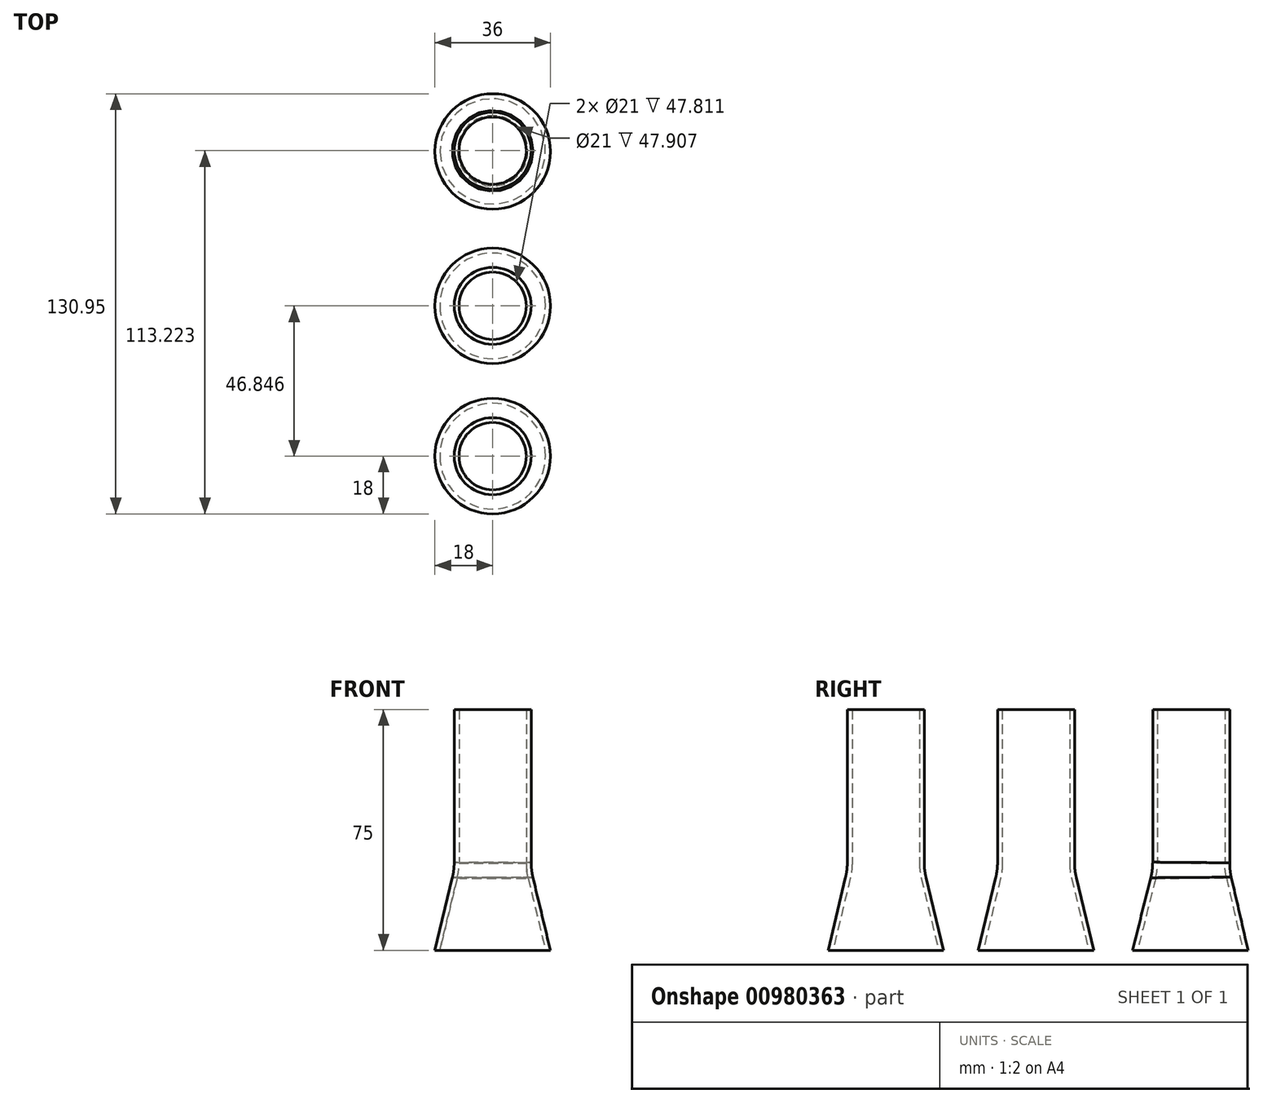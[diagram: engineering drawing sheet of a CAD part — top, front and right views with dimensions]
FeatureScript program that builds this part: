
annotation { "Feature Type Name" : "Feature", "Feature Type Description" : "" }
export const myFeature = defineFeature(function(context is Context, id is Id, definition is map)
    precondition{}
    {
        {
            var Q0;
            Q0=qCreatedBy(makeId("Top.planeOp"),FACE);
            var sketch = newSketch(context, id + "F0", { "sketchPlane" : qUnion([Q0])});
            skCircle(sketch, "E0", {"center": v(0, 0) * mm, "radius": 18 * mm});
            skSolve(sketch);
        }
        {
            var Q0;
            Q0=qCreatedBy(makeId("Top.planeOp"),FACE);
            cPlane(context, id + "F1", {"entities" : qUnion([Q0]), "cplaneType" : CPlaneType.OFFSET, "offset" : 25 * mm, "width" : 150 * mm, "height" : 150 * mm});
        }
        {
            var Q0;
            Q0=qCreatedBy(id+"F1.planeOp",FACE);
            var sketch = newSketch(context, id + "F2", { "sketchPlane" : qUnion([Q0])});
            skCircle(sketch, "E1", {"center": v(0, 0) * mm, "radius": 12 * mm});
            skSolve(sketch);
        }
        {
            var Q0;
            Q0=qCreatedBy(id+"F1.planeOp",FACE);
            cPlane(context, id + "F3", {"entities" : qUnion([Q0]), "cplaneType" : CPlaneType.OFFSET, "offset" : 50 * mm, "width" : 150 * mm, "height" : 150 * mm});
        }
        {
            var Q0;
            Q0 = qSketchRegion(id + "F0", true);
            var Q1;
            Q1 = qSketchRegion(id + "F2", true);
            loft(context, id + "F4", {"sheetProfilesArray" : [{ "sheetProfileEntities" : qUnion([Q0]) }, { "sheetProfileEntities" : qUnion([Q1]) }]});
        }
        {
            var Q0;
            Q0 = qSketchRegion(id + "F2", true);
            var Q1;
            Q1=qCreatedBy(id+"F3.planeOp",FACE);
            extrude(context, id + "F5", {"entities" : qUnion([Q0]), "operationType" : NewBodyOperationType.ADD, "endBound" : BoundingType.UP_TO_SURFACE, "depth" : 25 * mm, "endBoundEntityFace" : qUnion([Q1]), "offsetDistance" : 25 * mm});
        }
        {
            var Q0;
            Q0=makeQuery(id+"F5.opExtrude","CAP_FACE",FACE,{"disambiguationData":[OSD([sQuery(id+"F2.wireOp",EDGE,"E1")])],"isStart":false});
            var Q1;
            Q1=makeQuery(id+"F4.opLoft","CAP_FACE",FACE,{"disambiguationData":[OSD([makeQuery(id+"F0.imprint","IMPRINT",FACE,{"disambiguationData":[TD([[makeQuery(id+"F0.imprint","IMPRINT",EDGE,{"derivedFrom":sQuery(id+"F0.wireOp",EDGE,"E0")}),1.0]])]})])],"isStart":true});
            shell(context, id + "F6", {"entities" : qUnion([Q0, Q1]), "thickness" : 1.5 * mm});
        }
        {
            var Q0;
            Q0=qCreatedBy(makeId("Top.planeOp"),FACE);
            var sketch = newSketch(context, id + "F7", { "sketchPlane" : qUnion([Q0])});
            skCircle(sketch, "E2", {"center": v(0, 46.85) * mm, "radius": 18 * mm});
            skSolve(sketch);
        }
        {
            var Q0;
            Q0=qCreatedBy(id+"F1.planeOp",FACE);
            var sketch = newSketch(context, id + "F8", { "sketchPlane" : qUnion([Q0])});
            skCircle(sketch, "E3", {"center": v(0, 46.85) * mm, "radius": 12 * mm});
            skSolve(sketch);
        }
        {
            var Q0;
            Q0 = qSketchRegion(id + "F7", true);
            var Q1;
            Q1 = qSketchRegion(id + "F8", true);
            loft(context, id + "F9", {"sheetProfilesArray" : [{ "sheetProfileEntities" : qUnion([Q0]) }, { "sheetProfileEntities" : qUnion([Q1]) }]});
        }
        {
            var Q0;
            Q0=makeQuery(id+"F9.opLoft","CAP_FACE",FACE,{"disambiguationData":[OSD([makeQuery(id+"F8.imprint","IMPRINT",FACE,{"disambiguationData":[TD([[makeQuery(id+"F8.imprint","IMPRINT",EDGE,{"derivedFrom":sQuery(id+"F8.wireOp",EDGE,"E3")}),1.0]])]})])],"isStart":true});
            var Q1;
            Q1=qCreatedBy(id+"F3.planeOp",FACE);
            extrude(context, id + "F10", {"entities" : qUnion([Q0]), "operationType" : NewBodyOperationType.ADD, "endBound" : BoundingType.UP_TO_SURFACE, "depth" : 25 * mm, "endBoundEntityFace" : qUnion([Q1]), "offsetDistance" : 25 * mm});
        }
        {
            var Q0;
            Q0=makeQuery(id+"F10.opExtrude","CAP_FACE",FACE,{"disambiguationData":[OSD([makeQuery(id+"F8.imprint","IMPRINT",FACE,{"disambiguationData":[TD([[makeQuery(id+"F8.imprint","IMPRINT",EDGE,{"derivedFrom":sQuery(id+"F8.wireOp",EDGE,"E3")}),1.0]])]})])],"isStart":false});
            var Q1;
            Q1=makeQuery(id+"F9.opLoft","CAP_FACE",FACE,{"disambiguationData":[OSD([makeQuery(id+"F7.imprint","IMPRINT",FACE,{"disambiguationData":[TD([[makeQuery(id+"F7.imprint","IMPRINT",EDGE,{"derivedFrom":sQuery(id+"F7.wireOp",EDGE,"E2")}),1.0]])]})])],"isStart":true});
            shell(context, id + "F11", {"entities" : qUnion([Q0, Q1]), "thickness" : 1.5 * mm});
        }
        {
            var Q0;
            Q0=qCreatedBy(makeId("Top.planeOp"),FACE);
            var sketch = newSketch(context, id + "F12", { "sketchPlane" : qUnion([Q0])});
            skCircle(sketch, "E4", {"center": v(0, 94.95) * mm, "radius": 18 * mm});
            skSolve(sketch);
        }
        {
            var Q0;
            Q0=qCreatedBy(id+"F1.planeOp",FACE);
            var sketch = newSketch(context, id + "F13", { "sketchPlane" : qUnion([Q0])});
            skCircle(sketch, "E5", {"center": v(0, 95.22) * mm, "radius": 12 * mm});
            skSolve(sketch);
        }
        {
            var Q0;
            Q0 = qSketchRegion(id + "F12", true);
            var Q1;
            Q1 = qSketchRegion(id + "F13", true);
            loft(context, id + "F14", {"sheetProfilesArray" : [{ "sheetProfileEntities" : qUnion([Q0]) }, { "sheetProfileEntities" : qUnion([Q1]) }]});
        }
        {
            var Q0;
            Q0 = qSketchRegion(id + "F13", true);
            var Q1;
            Q1=qCreatedBy(id+"F3.planeOp",FACE);
            extrude(context, id + "F15", {"entities" : qUnion([Q0]), "operationType" : NewBodyOperationType.ADD, "endBound" : BoundingType.UP_TO_SURFACE, "depth" : 25 * mm, "endBoundEntityFace" : qUnion([Q1]), "offsetDistance" : 25 * mm});
        }
        {
            var Q0;
            Q0=makeQuery(id+"F14.opLoft","CAP_FACE",FACE,{"disambiguationData":[OSD([makeQuery(id+"F12.imprint","IMPRINT",FACE,{"disambiguationData":[TD([[makeQuery(id+"F12.imprint","IMPRINT",EDGE,{"derivedFrom":sQuery(id+"F12.wireOp",EDGE,"E4")}),1.0]])]})])],"isStart":true});
            var Q1;
            Q1=makeQuery(id+"F15.opExtrude","CAP_FACE",FACE,{"disambiguationData":[OSD([sQuery(id+"F13.wireOp",EDGE,"E5")])],"isStart":false});
            shell(context, id + "F16", {"entities" : qUnion([Q0, Q1]), "thickness" : 1.5 * mm});
        }
        {
            var Q0;
            {var subQ0=sQuery(id+"F2.wireOp",EDGE,"E1");Q0=makeQuery(id+"F5.boolean.opBoolean","MERGE",EDGE,{"derivedFrom":[makeQuery(id+"F4.opLoft","MID_CAP_EDGE",EDGE,{"disambiguationData":[OSD([subQ0])],"capPos":1.0}),makeQuery(id+"F5.opExtrude","CAP_EDGE",EDGE,{"disambiguationData":[OSD([subQ0])],"isStart":true})]});}
            var Q1;
            {var subQ0=sQuery(id+"F2.wireOp",EDGE,"E1");Q1=makeQuery(id+"F6.opShell","OFFSET_EDGE",EDGE,{"disambiguationData":[OSD([subQ0]),TDD([makeQuery(id+"F5.boolean.opBoolean","MERGE",EDGE,{"derivedFrom":[makeQuery(id+"F4.opLoft","MID_CAP_EDGE",EDGE,{"disambiguationData":[OSD([subQ0])],"capPos":1.0}),makeQuery(id+"F5.opExtrude","CAP_EDGE",EDGE,{"disambiguationData":[OSD([subQ0])],"isStart":true})]})])]});}
            var Q2;
            {var subQ0=sQuery(id+"F13.wireOp",EDGE,"E5");Q2=makeQuery(id+"F15.boolean.opBoolean","MERGE",EDGE,{"derivedFrom":[makeQuery(id+"F14.opLoft","MID_CAP_EDGE",EDGE,{"disambiguationData":[OSD([subQ0])],"capPos":1.0}),makeQuery(id+"F15.opExtrude","CAP_EDGE",EDGE,{"disambiguationData":[OSD([subQ0])],"isStart":true})]});}
            var Q3;
            {var subQ0=sQuery(id+"F8.wireOp",EDGE,"E3");Q3=makeQuery(id+"F10.boolean.opBoolean","MERGE",EDGE,{"derivedFrom":[makeQuery(id+"F9.opLoft","MID_CAP_EDGE",EDGE,{"disambiguationData":[OSD([subQ0])],"capPos":1.0}),makeQuery(id+"F10.opExtrude","CAP_EDGE",EDGE,{"disambiguationData":[OSD([subQ0])],"isStart":true})]});}
            var Q4;
            {var subQ0=sQuery(id+"F13.wireOp",EDGE,"E5");Q4=makeQuery(id+"F16.opShell","OFFSET_EDGE",EDGE,{"disambiguationData":[OSD([subQ0]),TDD([makeQuery(id+"F15.boolean.opBoolean","MERGE",EDGE,{"derivedFrom":[makeQuery(id+"F14.opLoft","MID_CAP_EDGE",EDGE,{"disambiguationData":[OSD([subQ0])],"capPos":1.0}),makeQuery(id+"F15.opExtrude","CAP_EDGE",EDGE,{"disambiguationData":[OSD([subQ0])],"isStart":true})]})])]});}
            var Q5;
            {var subQ0=sQuery(id+"F8.wireOp",EDGE,"E3");Q5=makeQuery(id+"F11.opShell","OFFSET_EDGE",EDGE,{"disambiguationData":[OSD([subQ0]),TDD([makeQuery(id+"F10.boolean.opBoolean","MERGE",EDGE,{"derivedFrom":[makeQuery(id+"F9.opLoft","MID_CAP_EDGE",EDGE,{"disambiguationData":[OSD([subQ0])],"capPos":1.0}),makeQuery(id+"F10.opExtrude","CAP_EDGE",EDGE,{"disambiguationData":[OSD([subQ0])],"isStart":true})]})])]});}
            fillet(context, id + "F17", {"entities" : qUnion([Q0, Q1, Q2, Q3, Q4, Q5]), "radius" : 20 * mm, "tangentPropagation" : true, "allowEdgeOverflow" : false});
        }
        {
            var Q0;
            Q0=qCreatedBy(makeId("Top.planeOp"),FACE);
            var sketch = newSketch(context, id + "F18", { "sketchPlane" : qUnion([Q0])});
            skLineSegment(sketch, "E6.bottom", {"start": v(19.85, 118.64) * mm, "end": v(-19.85, 118.64) * mm});
            skLineSegment(sketch, "E6.top", {"start": v(19.85, -24.56) * mm, "end": v(-19.85, -24.56) * mm});
            skLineSegment(sketch, "E6.left", {"start": v(19.85, 118.64) * mm, "end": v(19.85, -24.56) * mm});
            skLineSegment(sketch, "E6.right", {"start": v(-19.85, 118.64) * mm, "end": v(-19.85, -24.56) * mm});
            skPoint(sketch, "E6.middle", {"position": v(0, 47.04) * mm});
            skSolve(sketch);
        }
        {
            var Q0;
            Q0 = qSketchRegion(id + "F18", true);
            extrude(context, id + "F19", {"entities" : qUnion([Q0]), "depth" : 2 * mm, "offsetDistance" : 25 * mm});
        }
        {
            var Q0;
            Q0=makeQuery(id+"F4.opLoft","SWEPT_BODY",BODY,{"disambiguationData":[OSD([makeQuery(id+"F0.imprint","IMPRINT",FACE,{"disambiguationData":[TD([[makeQuery(id+"F0.imprint","IMPRINT",EDGE,{"derivedFrom":sQuery(id+"F0.wireOp",EDGE,"E0")}),1.0]])]}),makeQuery(id+"F2.imprint","IMPRINT",FACE,{"disambiguationData":[TD([[makeQuery(id+"F2.imprint","IMPRINT",EDGE,{"derivedFrom":sQuery(id+"F2.wireOp",EDGE,"E1")}),1.0]])]})])]});
            var Q1;
            Q1=makeQuery(id+"F9.opLoft","SWEPT_BODY",BODY,{"disambiguationData":[OSD([makeQuery(id+"F7.imprint","IMPRINT",FACE,{"disambiguationData":[TD([[makeQuery(id+"F7.imprint","IMPRINT",EDGE,{"derivedFrom":sQuery(id+"F7.wireOp",EDGE,"E2")}),1.0]])]}),makeQuery(id+"F8.imprint","IMPRINT",FACE,{"disambiguationData":[TD([[makeQuery(id+"F8.imprint","IMPRINT",EDGE,{"derivedFrom":sQuery(id+"F8.wireOp",EDGE,"E3")}),1.0]])]})])]});
            var Q2;
            Q2=makeQuery(id+"F14.opLoft","SWEPT_BODY",BODY,{"disambiguationData":[OSD([makeQuery(id+"F12.imprint","IMPRINT",FACE,{"disambiguationData":[TD([[makeQuery(id+"F12.imprint","IMPRINT",EDGE,{"derivedFrom":sQuery(id+"F12.wireOp",EDGE,"E4")}),1.0]])]}),makeQuery(id+"F13.imprint","IMPRINT",FACE,{"disambiguationData":[TD([[makeQuery(id+"F13.imprint","IMPRINT",EDGE,{"derivedFrom":sQuery(id+"F13.wireOp",EDGE,"E5")}),1.0]])]})])]});
            var Q3;
            Q3=makeQuery(id+"F19.opExtrude","SWEPT_BODY",BODY,{"disambiguationData":[OSD([sQuery(id+"F18.wireOp",EDGE,"E6.bottom"),sQuery(id+"F18.wireOp",EDGE,"E6.top"),sQuery(id+"F18.wireOp",EDGE,"E6.left"),sQuery(id+"F18.wireOp",EDGE,"E6.right")])]});
            booleanBodies(context, id + "F20", {"operationType" : BooleanOperationType.SUBTRACTION, "tools" : qUnion([Q0, Q1, Q2]), "targets" : qUnion([Q3]), "keepTools" : true});
        }
        {
            var Q0;
            Q0=makeQuery(id+"F20.opBoolean","SPLIT",BODY,{"disambiguationData":[OD(3.0)],"derivedFrom":makeQuery(id+"F19.opExtrude","SWEPT_BODY",BODY,{"disambiguationData":[OSD([sQuery(id+"F18.wireOp",EDGE,"E6.bottom"),sQuery(id+"F18.wireOp",EDGE,"E6.top"),sQuery(id+"F18.wireOp",EDGE,"E6.left"),sQuery(id+"F18.wireOp",EDGE,"E6.right")])]})});
            var Q1;
            Q1=makeQuery(id+"F20.opBoolean","SPLIT",BODY,{"disambiguationData":[OD(2.0)],"derivedFrom":makeQuery(id+"F19.opExtrude","SWEPT_BODY",BODY,{"disambiguationData":[OSD([sQuery(id+"F18.wireOp",EDGE,"E6.bottom"),sQuery(id+"F18.wireOp",EDGE,"E6.top"),sQuery(id+"F18.wireOp",EDGE,"E6.left"),sQuery(id+"F18.wireOp",EDGE,"E6.right")])]})});
            var Q2;
            Q2=makeQuery(id+"F20.opBoolean","SPLIT",BODY,{"disambiguationData":[OD(1.0)],"derivedFrom":makeQuery(id+"F19.opExtrude","SWEPT_BODY",BODY,{"disambiguationData":[OSD([sQuery(id+"F18.wireOp",EDGE,"E6.bottom"),sQuery(id+"F18.wireOp",EDGE,"E6.top"),sQuery(id+"F18.wireOp",EDGE,"E6.left"),sQuery(id+"F18.wireOp",EDGE,"E6.right")])]})});
            deleteBodies(context, id + "F21", {"entities" : qUnion([Q0, Q1, Q2])});
        }
    });
